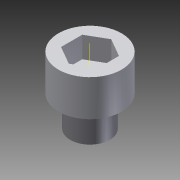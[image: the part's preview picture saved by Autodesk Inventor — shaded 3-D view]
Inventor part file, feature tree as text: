
AUTODESK INVENTOR PART (.ipt)
format: ipt  version: 2012 (Build 160160000, 160)  size: 159,232 bytes
history: native  units: mm
features: other x3, extrude x3, sketch x3, projected_geometry x3, fillet x2
ambient origin geometry x8: Origin, YZ Plane, XZ Plane, XY Plane, X Axis, Y Axis, Z Axis, Center Point
bodies: Solid1 (feature_tree)
feature tree (14):
  other  "ServoToScrewKey.ipt"
  extrude  "Extrusion1"  TaperAngle=0.0deg  [1 undecoded]
  extrude  "Extrusion2"  Depth=2.0mm
  extrude  "Extrusion4"  Depth=1.0mm
  fillet  "Fillet1"  Radius=4.0mm
  fillet  "Fillet2"  Radius=120.0mm
  other  "Solid2::ServoToScrewKey.ipt"
  other  "TaggingFeature1"
  sketch  "Sketch2"  dims[d0=10.0mm d1=0.0mm d2=0.0mm]
  projected_geometry  "Projected Loop1"
  sketch  "Sketch3"  dims[d3=10.0mm d4=0.0mm d15=2.0mm]
  projected_geometry  "Projected Loop2"
  sketch  "Sketch8"  dims[d16=1.0mm d17=1.0mm d18=4.0mm d19=120.0mm d21=360.0deg d23=10.0mm d24=0.0mm d25=0.5mm d26=0.5mm]
  projected_geometry  "Projected Loop6"
note: 1 required parameter value undecoded (feature->parameter linkage not recoverable at this tier; creation-order binding heuristic only, values carry confidence <= 0.55)
